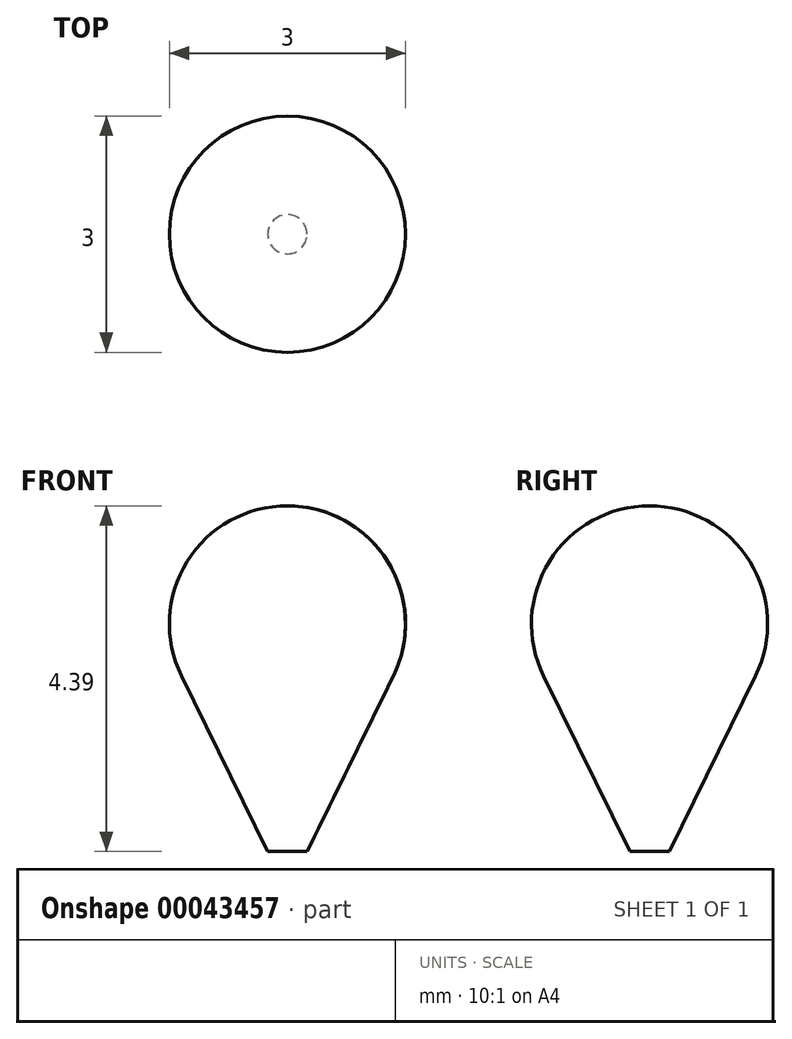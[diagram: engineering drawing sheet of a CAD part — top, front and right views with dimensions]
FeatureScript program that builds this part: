
annotation { "Feature Type Name" : "Feature", "Feature Type Description" : "" }
export const myFeature = defineFeature(function(context is Context, id is Id, definition is map)
    precondition{}
    {
        {
            var Q0;
            Q0=qCreatedBy(makeId("Front.planeOp"),FACE);
            var sketch = newSketch(context, id + "F0", { "sketchPlane" : qUnion([Q0])});
            skCircle(sketch, "E0", {"center": v(0, 0) * mm, "radius": 1.5 * mm});
            skLineSegment(sketch, "E1", {"start": v(0, -1.5) * mm, "end": v(0, -2.9) * mm});
            skLineSegment(sketch, "E2", {"start": v(0, -2.9) * mm, "end": v(-0.25, -2.9) * mm});
            skLineSegment(sketch, "E3", {"start": v(-0.25, -2.9) * mm, "end": v(-1.35, -0.66) * mm});
            skLineSegment(sketch, "E4.MirrorCS", {"start": v(0.25, -2.9) * mm, "end": v(1.35, -0.66) * mm});
            skLineSegment(sketch, "E5.MirrorCS", {"start": v(0, -2.9) * mm, "end": v(0.25, -2.9) * mm});
            skLineSegment(sketch, "E6", {"start": v(0, -1.5) * mm, "end": v(0, 1.5) * mm});
            skLineSegment(sketch, "E7", {"start": v(0, 1.97) * mm, "end": v(0, -3.4) * mm});
            skSolve(sketch);
        }
        {
            var Q0;
            {var subQ1=sQuery(id+"F0.wireOp",EDGE,"E0");var subQ4=makeQuery(id+"F0.imprint","INTERSECT",VERTEX,{"derivedFrom":[subQ1,sQuery(id+"F0.wireOp",EDGE,"E4.MirrorCS")]});Q0=makeQuery(id+"F0.imprint","IMPRINT",FACE,{"disambiguationData":[TD([[makeQuery(id+"F0.imprint","IMPRINT",EDGE,{"disambiguationData":[TD([[subQ4,1.0]])],"derivedFrom":subQ1}),1.0]])]});}
            var Q1;
            {var subQ4=sQuery(id+"F0.wireOp",EDGE,"E4.MirrorCS");Q1=makeQuery(id+"F0.imprint","IMPRINT",FACE,{"disambiguationData":[TD([[makeQuery(id+"F0.imprint","IMPRINT",EDGE,{"derivedFrom":subQ4}),1.0]])]});}
            var Q2;
            Q2=sQuery(id+"F0.wireOp",EDGE,"E7");
            revolve(context, id + "F1", {"entities" : qUnion([Q0, Q1]), "axis" : qUnion([Q2]), "revolveType" : RevolveType.FULL});
        }
    });
